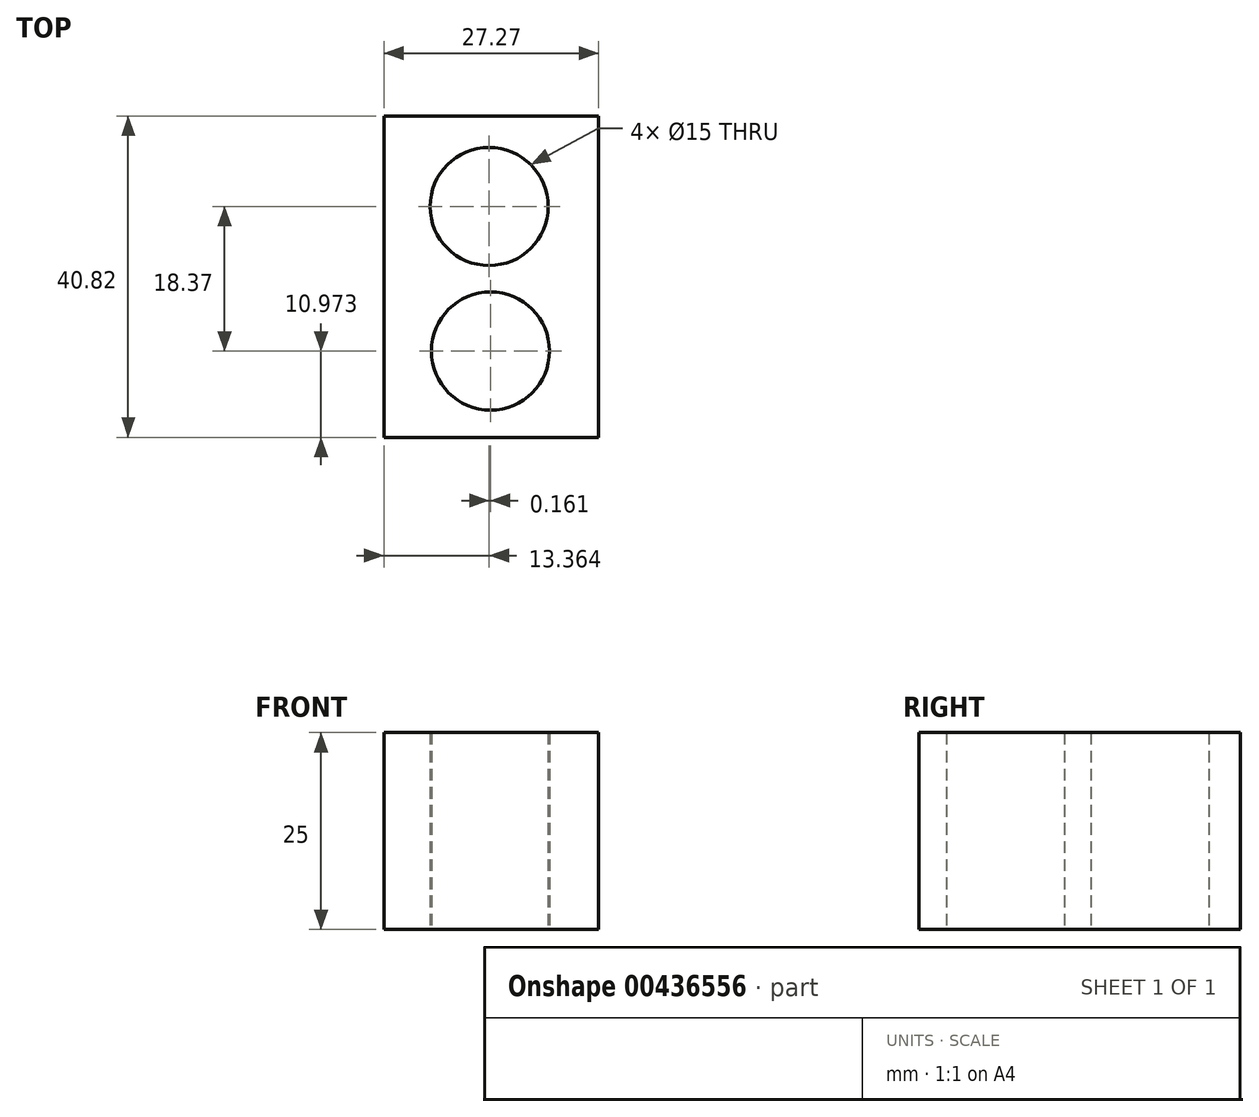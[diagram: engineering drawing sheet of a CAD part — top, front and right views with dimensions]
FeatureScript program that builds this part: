
annotation { "Feature Type Name" : "Feature", "Feature Type Description" : "" }
export const myFeature = defineFeature(function(context is Context, id is Id, definition is map)
    precondition{}
    {
        {
            var Q0;
            Q0=qCreatedBy(makeId("Top.planeOp"),FACE);
            var sketch = newSketch(context, id + "F0", { "sketchPlane" : qUnion([Q0])});
            skLineSegment(sketch, "E0.bottom", {"start": v(-13.73, 29.66) * mm, "end": v(13.54, 29.66) * mm});
            skLineSegment(sketch, "E0.top", {"start": v(-13.73, -11.16) * mm, "end": v(13.54, -11.16) * mm});
            skLineSegment(sketch, "E0.left", {"start": v(-13.73, 29.66) * mm, "end": v(-13.73, -11.16) * mm});
            skLineSegment(sketch, "E0.right", {"start": v(13.54, 29.66) * mm, "end": v(13.54, -11.16) * mm});
            skCircle(sketch, "E1", {"center": v(-0.2, -0.19) * mm, "radius": 7.5 * mm});
            skCircle(sketch, "E2", {"center": v(-0.37, 18.18) * mm, "radius": 7.5 * mm});
            skSolve(sketch);
        }
        {
            var Q0;
            Q0=makeQuery(id+"F0.imprint","IMPRINT",FACE,{"disambiguationData":[TD([[makeQuery(id+"F0.imprint","IMPRINT",EDGE,{"derivedFrom":sQuery(id+"F0.wireOp",EDGE,"E0.bottom")}),-1.0]])]});
            extrude(context, id + "F1", {"entities" : qUnion([Q0]), "depth" : 25 * mm});
        }
    });
